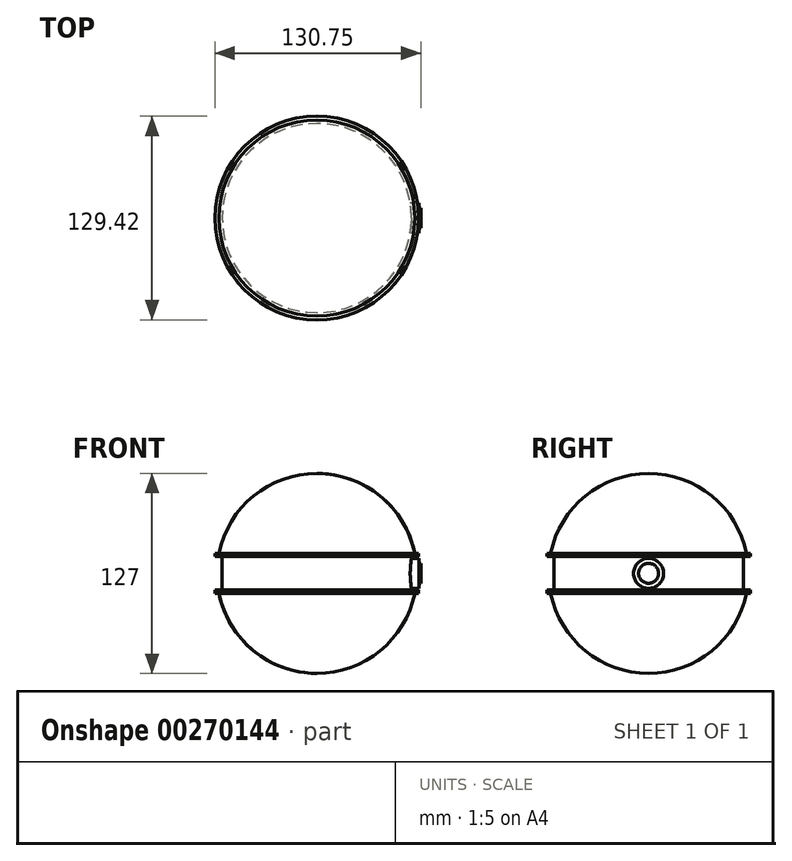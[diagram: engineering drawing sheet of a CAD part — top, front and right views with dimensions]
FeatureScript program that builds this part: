
annotation { "Feature Type Name" : "Feature", "Feature Type Description" : "" }
export const myFeature = defineFeature(function(context is Context, id is Id, definition is map)
    precondition{}
    {
        {
            var Q0;
            Q0=qCreatedBy(makeId("Front.planeOp"),FACE);
            var sketch = newSketch(context, id + "F0", { "sketchPlane" : qUnion([Q0])});
            skArc(sketch, "E0", {"start": v(0, 63.5) * mm, "mid": v(-40.16, 49.19) * mm, "end": v(-62.22, 12.7) * mm});
            skLineSegment(sketch, "E1", {"start": v(0, 63.5) * mm, "end": v(0, -63.5) * mm});
            skLineSegment(sketch, "E2", {"start": v(0, 0) * mm, "end": v(0, 12.7) * mm, "construction": true});
            skLineSegment(sketch, "E3", {"start": v(0, 12.7) * mm, "end": v(0, -12.7) * mm, "construction": true});
            skLineSegment(sketch, "E4", {"start": v(0, 12.7) * mm, "end": v(-62.22, 12.7) * mm});
            skLineSegment(sketch, "E5", {"start": v(0, -12.7) * mm, "end": v(-62.22, -12.7) * mm});
            skArc(sketch, "E6.trimOffspring", {"start": v(-62.22, -12.7) * mm, "mid": v(-40.16, -49.19) * mm, "end": v(0, -63.5) * mm});
            skLineSegment(sketch, "E7", {"start": v(-60.1, 12.7) * mm, "end": v(-60.1, -12.7) * mm});
            skLineSegment(sketch, "E8", {"start": v(-62.22, 12.7) * mm, "end": v(-64.71, 12.7) * mm});
            skLineSegment(sketch, "E9", {"start": v(-64.71, 12.7) * mm, "end": v(-64.55, 10.62) * mm});
            skLineSegment(sketch, "E10", {"start": v(-64.55, 10.62) * mm, "end": v(-60.1, 10.62) * mm});
            skLineSegment(sketch, "E11.MirrorCS", {"start": v(-64.55, -10.62) * mm, "end": v(-60.1, -10.62) * mm});
            skLineSegment(sketch, "E12.MirrorCS", {"start": v(-64.71, -12.7) * mm, "end": v(-64.55, -10.62) * mm});
            skLineSegment(sketch, "E13.MirrorCS", {"start": v(-62.22, -12.7) * mm, "end": v(-64.71, -12.7) * mm});
            skSolve(sketch);
        }
        {
            var Q0;
            Q0=qCreatedBy(makeId("Right.planeOp"),FACE);
            var sketch = newSketch(context, id + "F1", { "sketchPlane" : qUnion([Q0])});
            skCircle(sketch, "E14", {"center": v(0, 0) * mm, "radius": 6.35 * mm});
            skSolve(sketch);
        }
        {
            var Q0;
            Q0=makeQuery(id+"F1.imprint","IMPRINT",FACE,{"disambiguationData":[TD([[makeQuery(id+"F1.imprint","IMPRINT",EDGE,{"derivedFrom":sQuery(id+"F1.wireOp",EDGE,"E14")}),1.0]])]});
            extrude(context, id + "F2", {"entities" : qUnion([Q0]), "depth" : 66.04 * mm});
        }
        {
            var Q0;
            Q0 = qSketchRegion(id + "F0", true);
            var Q1;
            Q1=sQuery(id+"F0.wireOp",EDGE,"E1");
            revolve(context, id + "F3", {"operationType" : NewBodyOperationType.ADD, "entities" : qUnion([Q0]), "axis" : qUnion([Q1]), "revolveType" : RevolveType.FULL});
        }
        {
            var Q0;
            Q0=qCreatedBy(makeId("Right.planeOp"),FACE);
            var sketch = newSketch(context, id + "F4", { "sketchPlane" : qUnion([Q0])});
            skCircle(sketch, "E15", {"center": v(0, 0) * mm, "radius": 9.53 * mm});
            skSolve(sketch);
        }
        {
            var Q0;
            Q0 = qSketchRegion(id + "F4", true);
            extrude(context, id + "F5", {"entities" : qUnion([Q0]), "operationType" : NewBodyOperationType.ADD, "depth" : 64.77 * mm});
        }
    });
